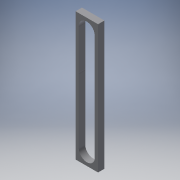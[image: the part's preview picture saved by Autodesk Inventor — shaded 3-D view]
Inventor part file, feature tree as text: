
AUTODESK INVENTOR PART (.ipt)
format: ipt  version: 2016 (Build 200138000, 138)  size: 113,152 bytes
history: native  units: in
note: dims shown in document units (in); Inventor stores cm internally (conversion verified against a paired STEP export)
features: reference x4, extrude x1, sketch x1
ambient origin geometry x8: Origin, YZ Plane, XZ Plane, XY Plane, X Axis, Y Axis, Z Axis, Center Point
bodies: Body1 (feature_tree)
feature tree (6):
  extrude  "Extrusion2"  Depth=0.0787in
  sketch  "Sketch1"  dims[d0=0.0787in d1=0.0787in d2=0.0787in d3=0.0787in d5=0.3937in d8=3.142in d9=2.591in d10=2.591in d11=0.1575in d12=0.0in]
  reference  "Reference1"
  reference  "Reference2"
  reference  "Reference3"
  reference  "Reference4"
